# Revit family: Access_Door-Removable_Door-Best Access Doors-Plastic-BA-PAC
name_source: partatom
category: Specialty Equipment
revit_build: Autodesk Revit 2017 (Build: 20160225_1515(x64)
units: mm (PartAtom-declared; Revit-internal decimal feet)

## family parameters
Cut with Voids When Loaded = No
Host = Face
OmniClass Number = 23.30.10.27.17
Part Type = Normal
Room Calculation Point = No
Round Connector Dimension = Use Diameter
Shared = No

## types (4) — shared parameters
Assembly Code = C1020700
Construction Material = Plastic - Best Access Doors - High Impact ABS
Default Elevation = 0"
Description = Removable plastic access door
Finish = Metal - Best Access Doors - Powder Coated White
Frame Depth = 5/8"
Manufacturer = Best Access Doors
Model = BA-PAC
Product data url = https://bimobject.com
URL = https://www.bestaccessdoors.com

## per-type parameters (varying)
| type | Door Height | Door Width | Frame Height | Frame Width |
| 6"x9" | 9" | 6" | 11 1/4" | 8 1/4" |
| 8"x8" | 8" | 8" | 10 1/4" | 10 1/4" |
| 14"x14" | 14" | 14" | 16 1/4" | 16 1/4" |
| 14"x29" | 29" | 14" | 31 1/4" | 16 1/4" |

## geometry (parser evidence)
native form markers: Blend x4, Sweep x4
no freeform markers — native parametric forms only
